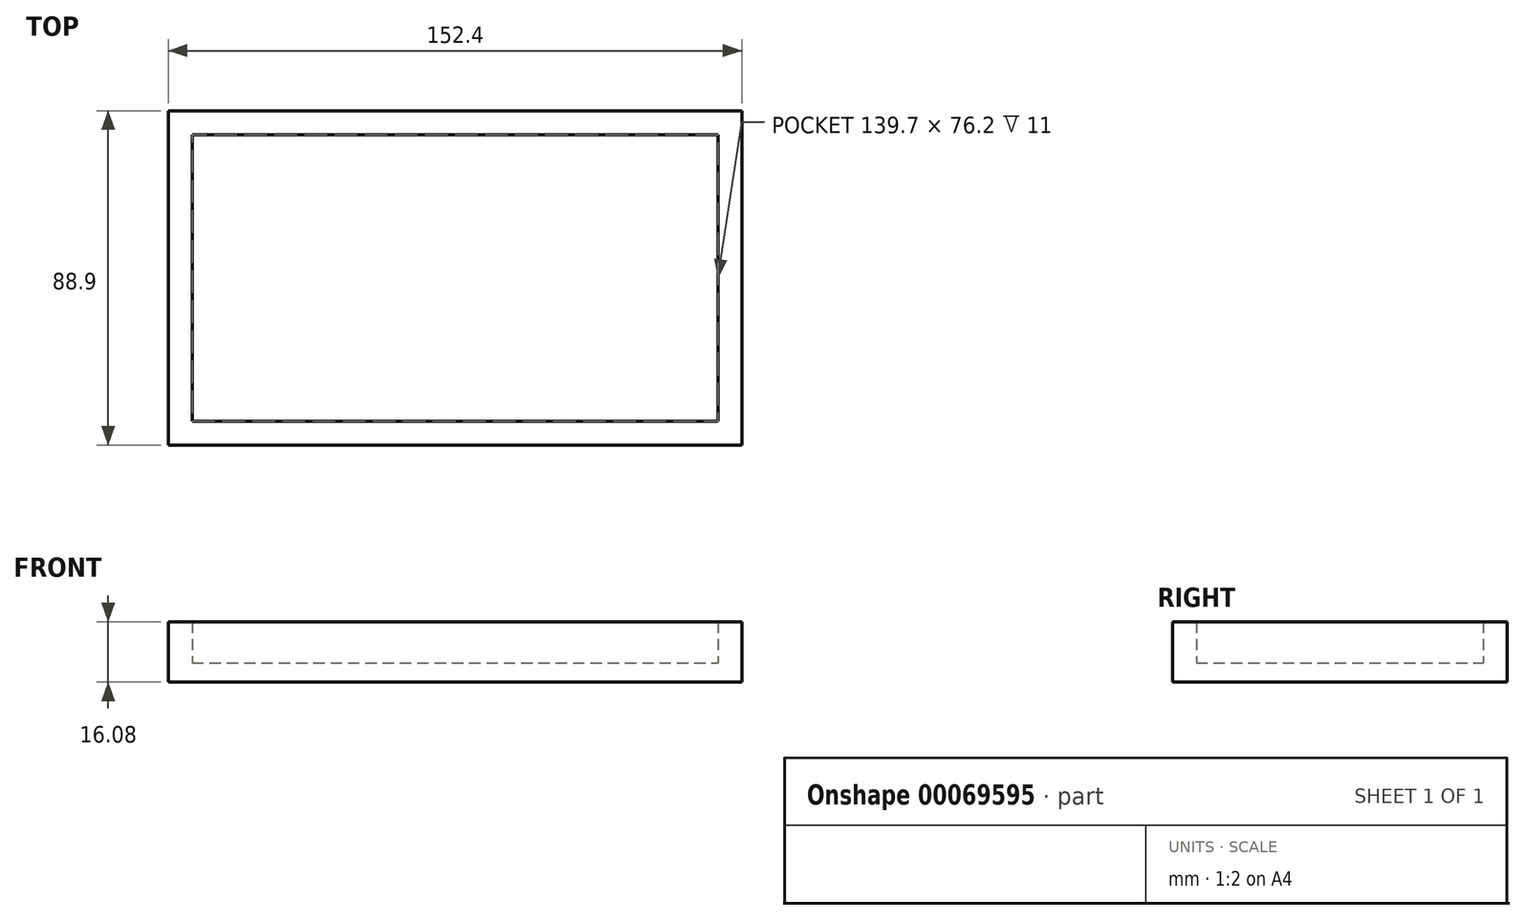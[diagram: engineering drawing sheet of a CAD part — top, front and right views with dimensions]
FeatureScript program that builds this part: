
annotation { "Feature Type Name" : "Feature", "Feature Type Description" : "" }
export const myFeature = defineFeature(function(context is Context, id is Id, definition is map)
    precondition{}
    {
        {
            var Q0;
            Q0=qCreatedBy(makeId("Top.planeOp"),FACE);
            var sketch = newSketch(context, id + "F0", { "sketchPlane" : qUnion([Q0])});
            skLineSegment(sketch, "E0", {"start": v(-76.2, 0) * mm, "end": v(76.2, 0) * mm});
            skLineSegment(sketch, "E1", {"start": v(-76.2, 0) * mm, "end": v(-76.2, 88.9) * mm});
            skLineSegment(sketch, "E2", {"start": v(-76.2, 88.9) * mm, "end": v(76.2, 88.9) * mm});
            skLineSegment(sketch, "E3", {"start": v(76.2, 0) * mm, "end": v(76.2, 88.9) * mm});
            skSolve(sketch);
        }
        {
            var Q0;
            Q0=makeQuery(id+"F0.imprint","IMPRINT",FACE,{"disambiguationData":[TD([[makeQuery(id+"F0.imprint","IMPRINT",EDGE,{"derivedFrom":sQuery(id+"F0.wireOp",EDGE,"E0")}),1.0]])]});
            extrude(context, id + "F1", {"entities" : qUnion([Q0]), "depth" : 5.08 * mm});
        }
        {
            var Q0;
            Q0=makeQuery(id+"F1.opExtrude","CAP_FACE",FACE,{"disambiguationData":[OSD([sQuery(id+"F0.wireOp",EDGE,"E0"),sQuery(id+"F0.wireOp",EDGE,"E1"),sQuery(id+"F0.wireOp",EDGE,"E2"),sQuery(id+"F0.wireOp",EDGE,"E3")])],"isStart":false});
            var sketch = newSketch(context, id + "F2", { "sketchPlane" : qUnion([Q0])});
            skPoint(sketch, "E4", {"position": v(76.2, 88.9) * mm});
            skPoint(sketch, "E5", {"position": v(76.2, 0) * mm});
            skPoint(sketch, "E6", {"position": v(-76.2, 0) * mm});
            skPoint(sketch, "E7", {"position": v(-76.2, 88.9) * mm});
            skPoint(sketch, "E8", {"position": v(0, 88.9) * mm});
            skPoint(sketch, "E9", {"position": v(76.2, 44.45) * mm});
            skPoint(sketch, "E10", {"position": v(-76.2, 44.45) * mm});
            skPoint(sketch, "E11", {"position": v(0, 0) * mm});
            skLineSegment(sketch, "E12", {"start": v(0, 0) * mm, "end": v(-76.2, 0) * mm});
            skLineSegment(sketch, "E13", {"start": v(-76.2, 0) * mm, "end": v(-76.2, 44.45) * mm});
            skLineSegment(sketch, "E14", {"start": v(-76.2, 44.45) * mm, "end": v(-76.2, 88.9) * mm});
            skLineSegment(sketch, "E15", {"start": v(-76.2, 88.9) * mm, "end": v(0, 88.9) * mm});
            skLineSegment(sketch, "E16", {"start": v(0, 88.9) * mm, "end": v(76.2, 88.9) * mm});
            skLineSegment(sketch, "E17", {"start": v(76.2, 88.9) * mm, "end": v(76.2, 44.45) * mm});
            skLineSegment(sketch, "E18", {"start": v(76.2, 44.45) * mm, "end": v(76.2, 0) * mm});
            skLineSegment(sketch, "E19", {"start": v(76.2, 0) * mm, "end": v(0, 0) * mm});
            skPoint(sketch, "E20", {"position": v(-38.1, 88.9) * mm});
            skPoint(sketch, "E21", {"position": v(38.1, 88.9) * mm});
            skPoint(sketch, "E22", {"position": v(38.1, 0) * mm});
            skPoint(sketch, "E23", {"position": v(-38.1, 0) * mm});
            skLineSegment(sketch, "E24", {"start": v(-69.85, 82.55) * mm, "end": v(69.85, 82.55) * mm});
            skLineSegment(sketch, "E25", {"start": v(-69.85, 6.35) * mm, "end": v(-69.85, 82.55) * mm});
            skLineSegment(sketch, "E26", {"start": v(-69.85, 6.35) * mm, "end": v(69.85, 6.35) * mm});
            skLineSegment(sketch, "E27", {"start": v(69.85, 6.35) * mm, "end": v(69.85, 82.55) * mm});
            skSolve(sketch);
        }
        {
            var Q0;
            Q0=makeQuery(id+"F2.imprint","IMPRINT",FACE,{"disambiguationData":[TD([[makeQuery(id+"F2.imprint","IMPRINT",EDGE,{"derivedFrom":sQuery(id+"F2.wireOp",EDGE,"E12")}),1.0]])]});
            extrude(context, id + "F3", {"entities" : qUnion([Q0]), "operationType" : NewBodyOperationType.ADD, "depth" : 11 * mm});
        }
    });
